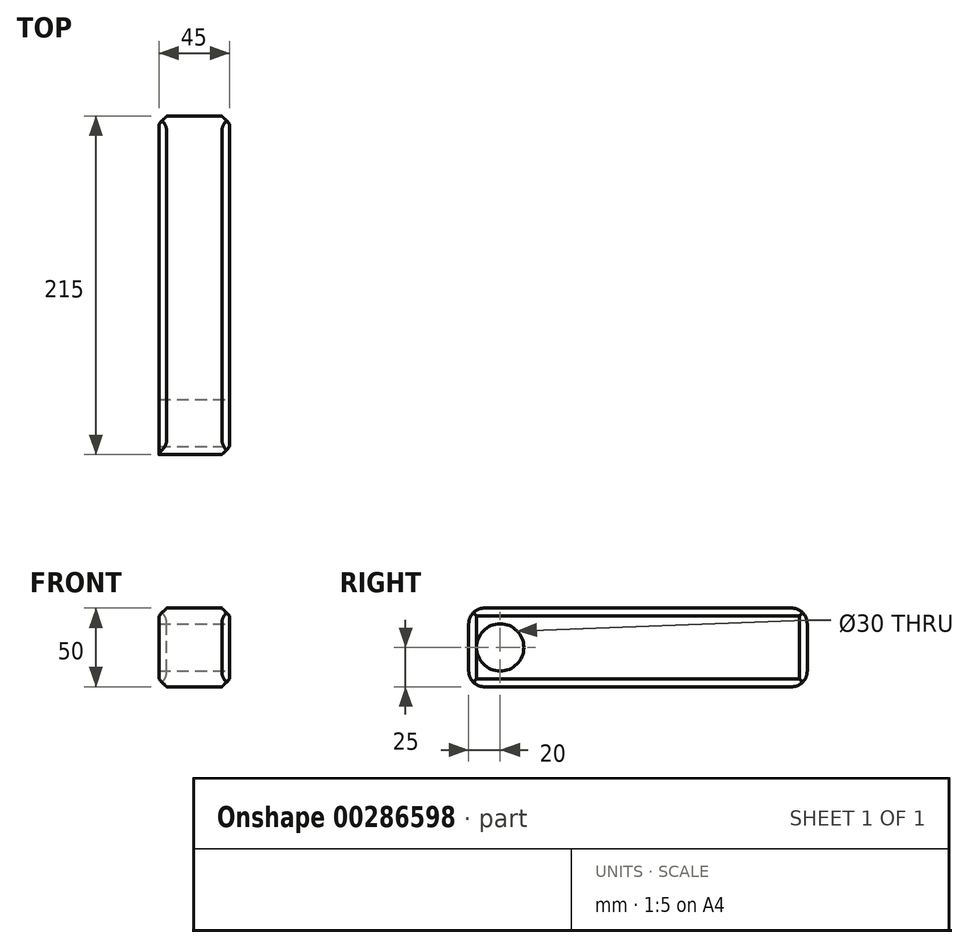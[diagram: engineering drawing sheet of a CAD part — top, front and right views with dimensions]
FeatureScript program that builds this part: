
annotation { "Feature Type Name" : "Feature", "Feature Type Description" : "" }
export const myFeature = defineFeature(function(context is Context, id is Id, definition is map)
    precondition{}
    {
        {
            var Q0;
            Q0=qCreatedBy(makeId("Front.planeOp"),FACE);
            var sketch = newSketch(context, id + "F0", { "sketchPlane" : qUnion([Q0])});
            skLineSegment(sketch, "E0.bottom", {"start": v(-22.5, 25) * mm, "end": v(22.5, 25) * mm});
            skLineSegment(sketch, "E0.top", {"start": v(-22.5, -25) * mm, "end": v(22.5, -25) * mm});
            skLineSegment(sketch, "E0.left", {"start": v(-22.5, 25) * mm, "end": v(-22.5, -25) * mm});
            skLineSegment(sketch, "E0.right", {"start": v(22.5, 25) * mm, "end": v(22.5, -25) * mm});
            skPoint(sketch, "E0.middle", {"position": v(0, 0) * mm});
            skSolve(sketch);
        }
        {
            var Q0;
            Q0=makeQuery(id+"F0.imprint","IMPRINT",FACE,{"disambiguationData":[TD([[makeQuery(id+"F0.imprint","IMPRINT",EDGE,{"derivedFrom":sQuery(id+"F0.wireOp",EDGE,"E0.bottom")}),-1.0]])]});
            extrude(context, id + "F1", {"entities" : qUnion([Q0]), "depth" : 215 * mm});
        }
        {
            var Q0;
            Q0=makeQuery(id+"F1.opExtrude","SWEPT_EDGE",EDGE,{"disambiguationData":[OSD([sQuery(id+"F0.wireOp",EDGE,"E0.bottom"),sQuery(id+"F0.wireOp",EDGE,"E0.right")])]});
            var Q1;
            Q1=makeQuery(id+"F1.opExtrude","SWEPT_EDGE",EDGE,{"disambiguationData":[OSD([sQuery(id+"F0.wireOp",EDGE,"E0.bottom"),sQuery(id+"F0.wireOp",EDGE,"E0.left")])]});
            var Q2;
            Q2=makeQuery(id+"F1.opExtrude","SWEPT_EDGE",EDGE,{"disambiguationData":[OSD([sQuery(id+"F0.wireOp",EDGE,"E0.top"),sQuery(id+"F0.wireOp",EDGE,"E0.right")])]});
            var Q3;
            Q3=makeQuery(id+"F1.opExtrude","SWEPT_EDGE",EDGE,{"disambiguationData":[OSD([sQuery(id+"F0.wireOp",EDGE,"E0.top"),sQuery(id+"F0.wireOp",EDGE,"E0.left")])]});
            var Q4;
            Q4=makeQuery(id+"F1.opExtrude","CAP_EDGE",EDGE,{"disambiguationData":[OSD([sQuery(id+"F0.wireOp",EDGE,"E0.right")])],"isStart":false});
            var Q5;
            Q5=makeQuery(id+"F1.opExtrude","CAP_EDGE",EDGE,{"disambiguationData":[OSD([sQuery(id+"F0.wireOp",EDGE,"E0.right")])],"isStart":true});
            var Q6;
            Q6=makeQuery(id+"F1.opExtrude","CAP_EDGE",EDGE,{"disambiguationData":[OSD([sQuery(id+"F0.wireOp",EDGE,"E0.left")])],"isStart":true});
            chamfer(context, id + "F2", {"entities" : qUnion([Q0, Q1, Q2, Q3, Q4, Q5, Q6]), "width" : 5 * mm, "tangentPropagation" : true});
        }
        {
            var Q0;
            Q0=makeQuery(id+"F1.opExtrude","CAP_EDGE",EDGE,{"disambiguationData":[OSD([sQuery(id+"F0.wireOp",EDGE,"E0.bottom")])],"isStart":false});
            var Q1;
            Q1=makeQuery(id+"F1.opExtrude","CAP_EDGE",EDGE,{"disambiguationData":[OSD([sQuery(id+"F0.wireOp",EDGE,"E0.top")])],"isStart":false});
            var Q2;
            Q2=makeQuery(id+"F1.opExtrude","CAP_EDGE",EDGE,{"disambiguationData":[OSD([sQuery(id+"F0.wireOp",EDGE,"E0.bottom")])],"isStart":true});
            var Q3;
            Q3=makeQuery(id+"F1.opExtrude","CAP_EDGE",EDGE,{"disambiguationData":[OSD([sQuery(id+"F0.wireOp",EDGE,"E0.top")])],"isStart":true});
            fillet(context, id + "F3", {"entities" : qUnion([Q0, Q1, Q2, Q3]), "radius" : 10 * mm, "tangentPropagation" : true, "allowEdgeOverflow" : false});
        }
        {
            var Q0;
            Q0=makeQuery(id+"F1.opExtrude","SWEPT_FACE",FACE,{"disambiguationData":[OSD([sQuery(id+"F0.wireOp",EDGE,"E0.right")])]});
            var sketch = newSketch(context, id + "F4", { "sketchPlane" : qUnion([Q0])});
            skCircle(sketch, "E1", {"center": v(-195, 0) * mm, "radius": 15 * mm});
            skSolve(sketch);
        }
        {
            var Q0;
            {var subQ0=sQuery(id+"F4.wireOp",EDGE,"E1");var subQ1=sQuery(id+"F0.wireOp",EDGE,"E0.right");var subQ2=makeQuery(id+"F1.opExtrude","SWEPT_FACE",FACE,{"disambiguationData":[OSD([subQ1])]});var subQ8=makeQuery(id+"F4.imprint","INTERSECT",VERTEX,{"derivedFrom":[makeQuery(id+"F2.opChamfer","BLEND_EDGE",EDGE,{"blendedFrom":[makeQuery(id+"F1.opExtrude","CAP_EDGE",EDGE,{"disambiguationData":[OSD([subQ1])],"isStart":false}),subQ2],"blendedInto":[subQ2]}),subQ0]});Q0=makeQuery(id+"F4.imprint","IMPRINT",FACE,{"disambiguationData":[TD([[makeQuery(id+"F4.imprint","IMPRINT",EDGE,{"disambiguationData":[TD([[subQ8,1.0]])],"derivedFrom":subQ0}),1.0]])]});}
            extrude(context, id + "F5", {"entities" : qUnion([Q0]), "operationType" : NewBodyOperationType.REMOVE, "endBound" : BoundingType.THROUGH_ALL, "oppositeDirection" : true, "depth" : 25 * mm});
        }
    });
